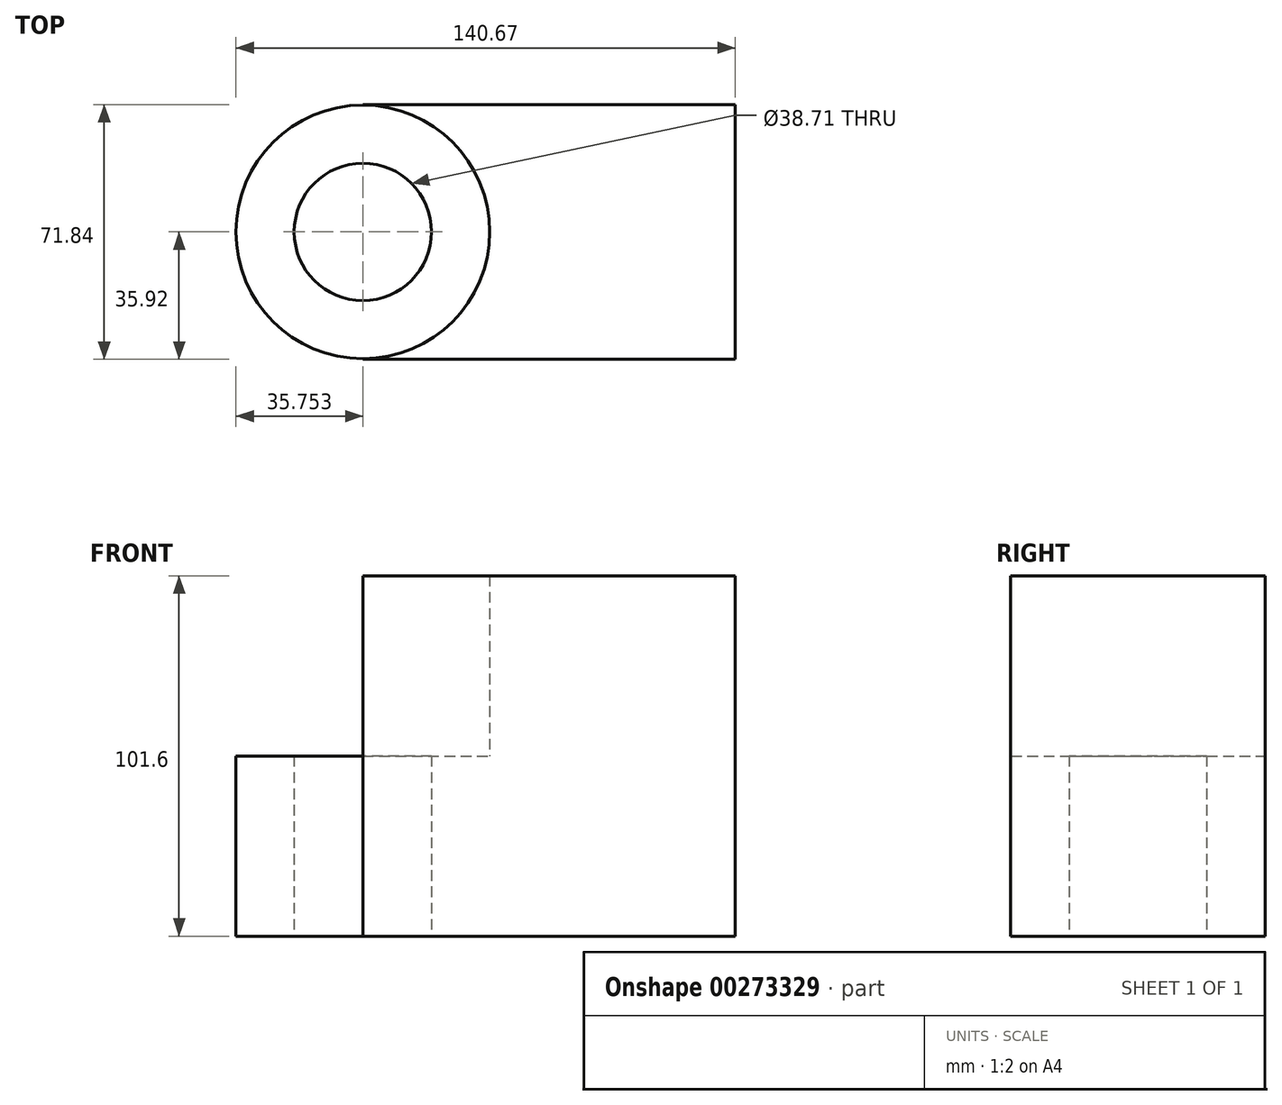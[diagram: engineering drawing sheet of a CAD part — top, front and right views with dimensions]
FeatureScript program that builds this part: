
annotation { "Feature Type Name" : "Feature", "Feature Type Description" : "" }
export const myFeature = defineFeature(function(context is Context, id is Id, definition is map)
    precondition{}
    {
        {
            var Q0;
            Q0=qCreatedBy(makeId("Top.planeOp"),FACE);
            var sketch = newSketch(context, id + "F0", { "sketchPlane" : qUnion([Q0])});
            skLineSegment(sketch, "E0.bottom", {"start": v(52.46, -35.92) * mm, "end": v(-52.46, -35.92) * mm});
            skLineSegment(sketch, "E0.top", {"start": v(52.46, 35.92) * mm, "end": v(-52.46, 35.92) * mm});
            skLineSegment(sketch, "E0.left", {"start": v(52.46, -35.92) * mm, "end": v(52.46, 35.92) * mm});
            skLineSegment(sketch, "E0.right", {"start": v(-52.46, -35.92) * mm, "end": v(-52.46, 35.92) * mm});
            skPoint(sketch, "E0.middle", {"position": v(0, 0) * mm});
            skCircle(sketch, "E1", {"center": v(-52.46, 0) * mm, "radius": 35.75 * mm});
            skCircle(sketch, "E2", {"center": v(-52.46, 0) * mm, "radius": 19.36 * mm});
            skSolve(sketch);
        }
        {
            var Q0;
            Q0 = qSketchRegion(id + "F0", true);
            extrude(context, id + "F1", {"entities" : qUnion([Q0]), "depth" : 50.8 * mm});
        }
        {
            var Q0;
            {var subQ0=sQuery(id+"F0.wireOp",EDGE,"E1");var subQ1=sQuery(id+"F0.wireOp",EDGE,"E0.right");var subQ2=makeQuery(id+"F0.imprint","INTERSECT",VERTEX,{"disambiguationData":[OD(0.0)],"derivedFrom":[subQ1,subQ0]});Q0=makeQuery(id+"F0.imprint","IMPRINT",FACE,{"disambiguationData":[TD([[makeQuery(id+"F0.imprint","IMPRINT",EDGE,{"disambiguationData":[TD([[subQ2,-1.0]])],"derivedFrom":subQ1}),1.0]])]});}
            var Q1;
            {var subQ0=sQuery(id+"F0.wireOp",EDGE,"E1");var subQ1=sQuery(id+"F0.wireOp",EDGE,"E0.right");var subQ2=makeQuery(id+"F0.imprint","INTERSECT",VERTEX,{"disambiguationData":[OD(0.0)],"derivedFrom":[subQ1,subQ0]});Q1=makeQuery(id+"F0.imprint","IMPRINT",FACE,{"disambiguationData":[TD([[makeQuery(id+"F0.imprint","IMPRINT",EDGE,{"disambiguationData":[TD([[subQ2,-1.0]])],"derivedFrom":subQ1}),-1.0]])]});}
            extrude(context, id + "F2", {"entities" : qUnion([Q0, Q1]), "operationType" : NewBodyOperationType.ADD, "depth" : 101.6 * mm});
        }
    });
